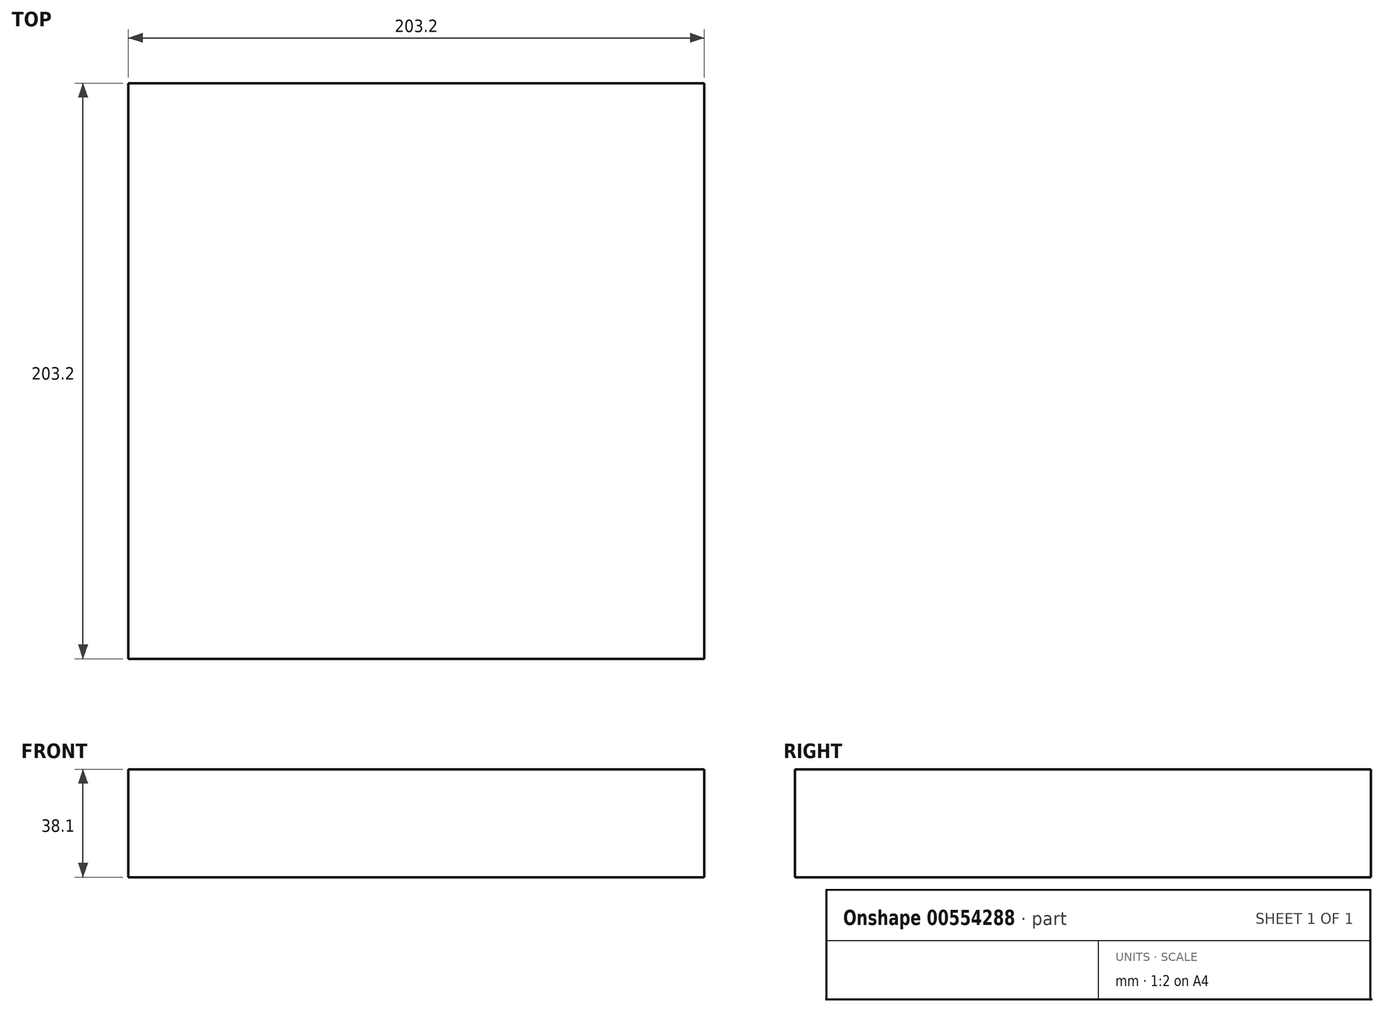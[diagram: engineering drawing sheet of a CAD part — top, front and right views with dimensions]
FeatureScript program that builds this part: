
annotation { "Feature Type Name" : "Feature", "Feature Type Description" : "" }
export const myFeature = defineFeature(function(context is Context, id is Id, definition is map)
    precondition{}
    {
        {
            var Q0;
            Q0=qCreatedBy(makeId("Top.planeOp"),FACE);
            var sketch = newSketch(context, id + "F0", { "sketchPlane" : qUnion([Q0])});
            skLineSegment(sketch, "E0.bottom", {"start": v(101.6, 101.6) * mm, "end": v(-101.6, 101.6) * mm});
            skLineSegment(sketch, "E0.top", {"start": v(101.6, -101.6) * mm, "end": v(-101.6, -101.6) * mm});
            skLineSegment(sketch, "E0.left", {"start": v(101.6, 101.6) * mm, "end": v(101.6, -101.6) * mm});
            skLineSegment(sketch, "E0.right", {"start": v(-101.6, 101.6) * mm, "end": v(-101.6, -101.6) * mm});
            skPoint(sketch, "E0.middle", {"position": v(0, 0) * mm});
            skSolve(sketch);
        }
        {
            var Q0;
            Q0=makeQuery(id+"F0.imprint","IMPRINT",FACE,{"disambiguationData":[TD([[makeQuery(id+"F0.imprint","IMPRINT",EDGE,{"derivedFrom":sQuery(id+"F0.wireOp",EDGE,"E0.bottom")}),1.0]])]});
            extrude(context, id + "F1", {"entities" : qUnion([Q0]), "depth" : 38.1 * mm, "offsetDistance" : 25.4 * mm});
        }
    });
